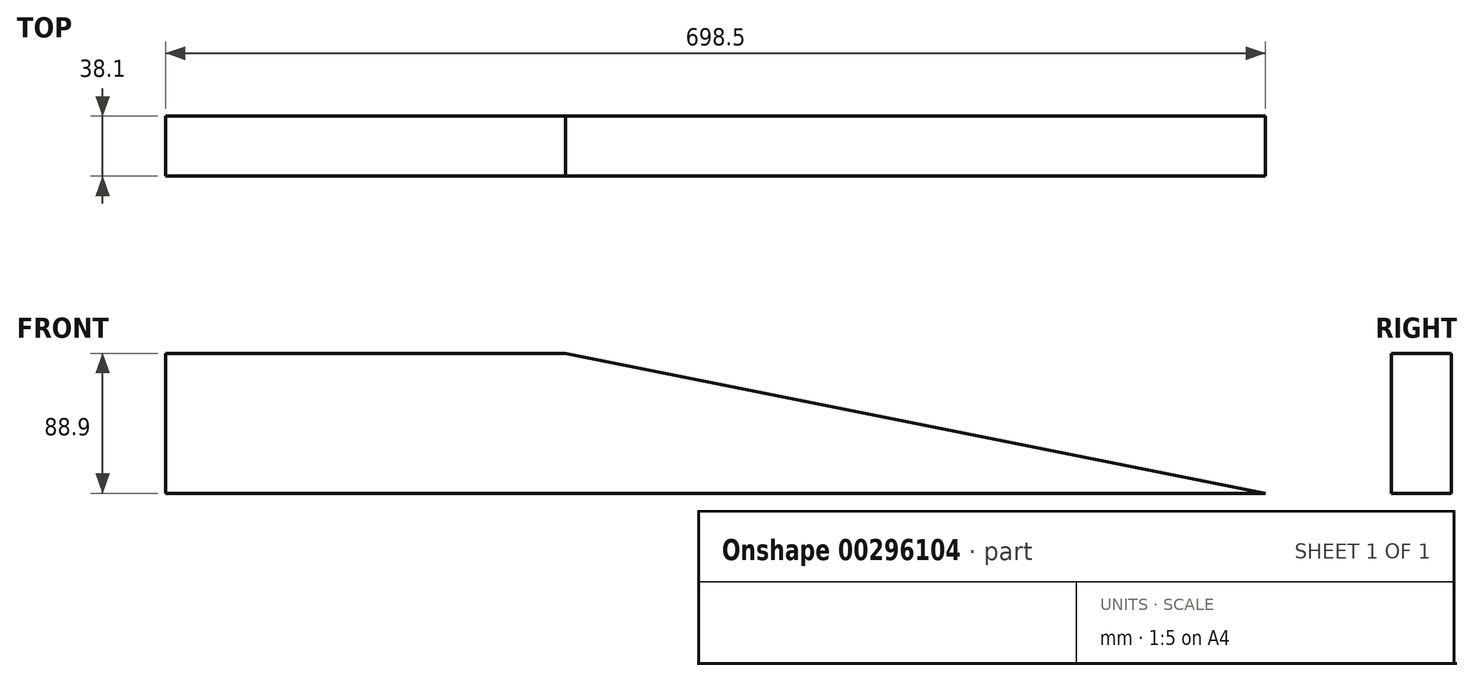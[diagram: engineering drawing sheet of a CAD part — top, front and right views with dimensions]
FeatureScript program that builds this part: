
annotation { "Feature Type Name" : "Feature", "Feature Type Description" : "" }
export const myFeature = defineFeature(function(context is Context, id is Id, definition is map)
    precondition{}
    {
        {
            var Q0;
            Q0=qCreatedBy(makeId("Front.planeOp"),FACE);
            var sketch = newSketch(context, id + "F0", { "sketchPlane" : qUnion([Q0])});
            skLineSegment(sketch, "E0", {"start": v(0, 0) * mm, "end": v(-444.5, 88.9) * mm});
            skLineSegment(sketch, "E1", {"start": v(-444.5, 88.9) * mm, "end": v(-698.5, 88.9) * mm});
            skLineSegment(sketch, "E2", {"start": v(-698.5, 88.9) * mm, "end": v(-698.5, 0) * mm});
            skLineSegment(sketch, "E3", {"start": v(-698.5, 0) * mm, "end": v(0, 0) * mm});
            skSolve(sketch);
        }
        {
            var Q0;
            Q0=makeQuery(id+"F0.imprint","IMPRINT",FACE,{"disambiguationData":[TD([[makeQuery(id+"F0.imprint","IMPRINT",EDGE,{"derivedFrom":sQuery(id+"F0.wireOp",EDGE,"E0")}),1.0]])]});
            extrude(context, id + "F1", {"entities" : qUnion([Q0]), "depth" : 38.1 * mm});
        }
    });
